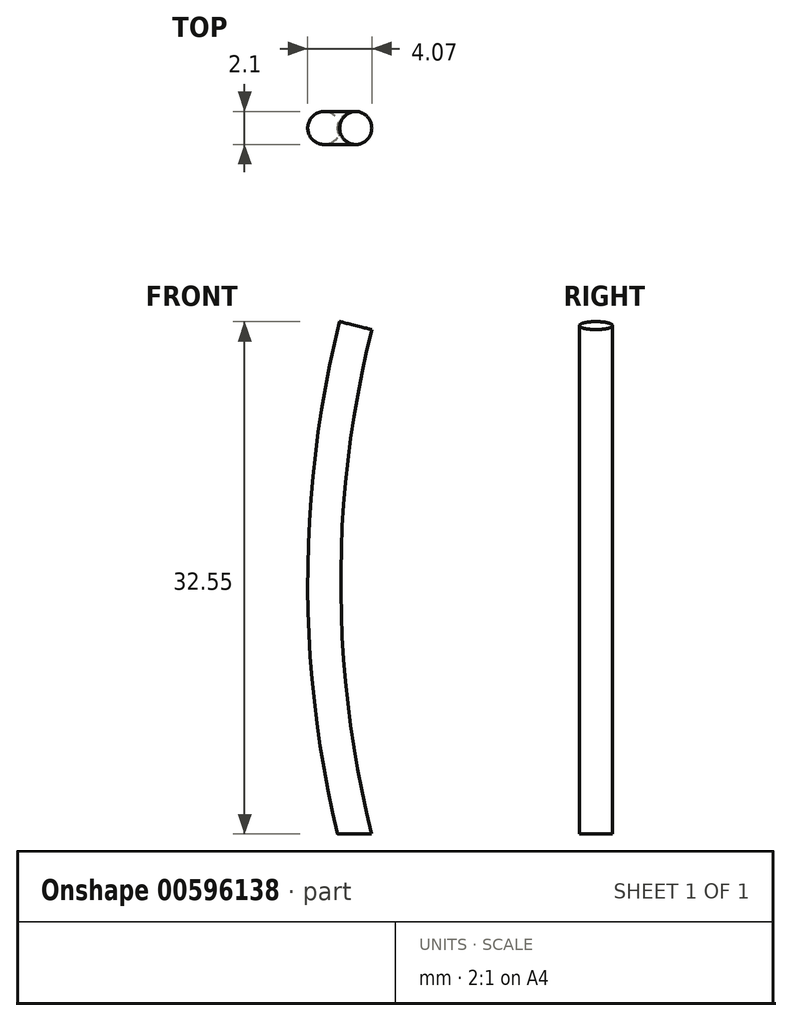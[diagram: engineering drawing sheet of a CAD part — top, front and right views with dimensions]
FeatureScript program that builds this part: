
annotation { "Feature Type Name" : "Feature", "Feature Type Description" : "" }
export const myFeature = defineFeature(function(context is Context, id is Id, definition is map)
    precondition{}
    {
        {
            var Q0;
            Q0=qCreatedBy(makeId("Front.planeOp"),FACE);
            var sketch = newSketch(context, id + "F0", { "sketchPlane" : qUnion([Q0])});
            skLineSegment(sketch, "E0", {"start": v(0, 0) * mm, "end": v(0, 16.3) * mm, "construction": true});
            skLineSegment(sketch, "E1", {"start": v(0, 0) * mm, "end": v(0, -16.3) * mm, "construction": true});
            skLineSegment(sketch, "E2", {"start": v(0, 0) * mm, "end": v(-2, 0) * mm, "construction": true});
            skArc(sketch, "E3", {"start": v(0, 16.3) * mm, "mid": v(-2, 0) * mm, "end": v(0, -16.3) * mm});
            skSolve(sketch);
        }
        {
            var Q0;
            Q0=qCreatedBy(makeId("Top.planeOp"),FACE);
            var sketch = newSketch(context, id + "F1", { "sketchPlane" : qUnion([Q0])});
            skPoint(sketch, "E4.0", {"position": v(-2, 0) * mm});
            skCircle(sketch, "E5", {"center": v(-2, 0) * mm, "radius": 1.05 * mm});
            skSolve(sketch);
        }
        {
            var Q0;
            Q0=makeQuery(id+"F1.imprint","IMPRINT",FACE,{"disambiguationData":[TD([[makeQuery(id+"F1.imprint","IMPRINT",EDGE,{"derivedFrom":sQuery(id+"F1.wireOp",EDGE,"E5")}),1.0]])]});
            var Q1;
            Q1=sQuery(id+"F0.wireOp",EDGE,"E3");
            sweep(context, id + "F2", {"profiles" : qUnion([Q0]), "path" : qUnion([Q1])});
        }
        {
            var Q0;
            Q0=qCreatedBy(makeId("Top.planeOp"),FACE);
            cPlane(context, id + "F3", {"entities" : qUnion([Q0]), "cplaneType" : CPlaneType.OFFSET, "offset" : 16 * mm, "oppositeDirection" : true, "width" : 150 * mm, "height" : 150 * mm});
        }
        {
            var Q0;
            Q0=qCreatedBy(id+"F3.planeOp",FACE);
            var sketch = newSketch(context, id + "F4", { "sketchPlane" : qUnion([Q0])});
            skCircle(sketch, "E6", {"center": v(0, 17.57) * mm, "radius": 29.2 * mm});
            skSolve(sketch);
        }
        {
            var Q0;
            Q0=makeQuery(id+"F4.imprint","IMPRINT",FACE,{"disambiguationData":[TD([[makeQuery(id+"F4.imprint","IMPRINT",EDGE,{"derivedFrom":sQuery(id+"F4.wireOp",EDGE,"E6")}),1.0]])]});
            extrude(context, id + "F5", {"entities" : qUnion([Q0]), "operationType" : NewBodyOperationType.REMOVE, "oppositeDirection" : true, "depth" : 25 * mm, "offsetDistance" : 25 * mm});
        }
    });
